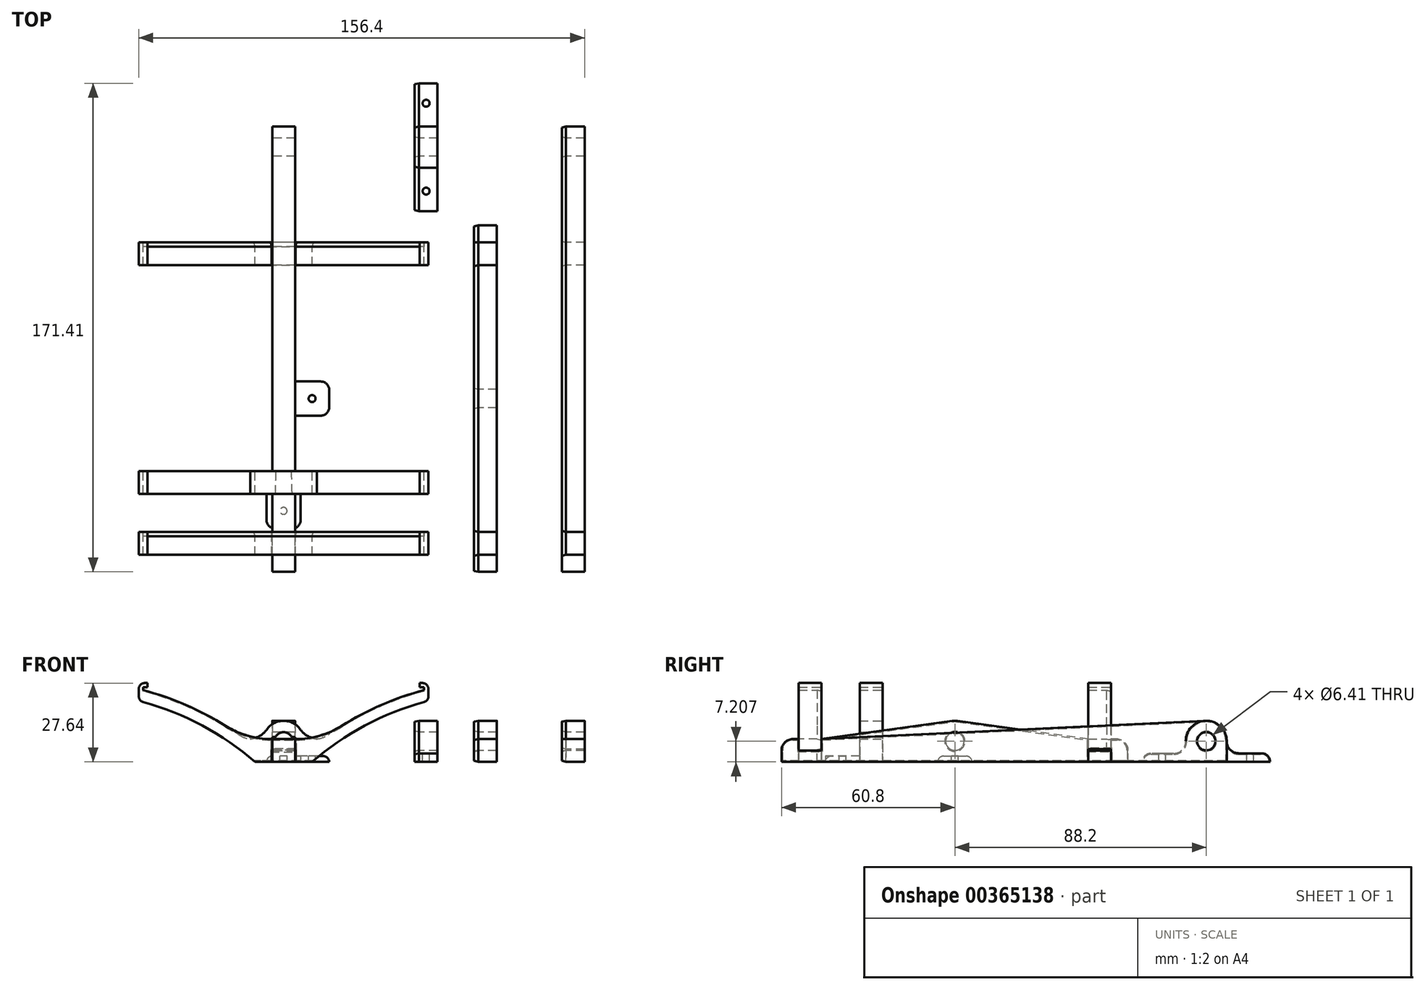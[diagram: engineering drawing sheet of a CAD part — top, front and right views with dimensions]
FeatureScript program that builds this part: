
annotation { "Feature Type Name" : "Feature", "Feature Type Description" : "" }
export const myFeature = defineFeature(function(context is Context, id is Id, definition is map)
    precondition{}
    {
        {
            assignVariable(context, id + "F0", {"name" : "frameWidth", "anyValue" : 101.6 * mm});
        }
        {
            assignVariable(context, id + "F1", {"name" : "picWidth", "anyValue" : 152.4 * mm});
        }
        {
            var Q0;
            Q0=qCreatedBy(makeId("Front.planeOp"),FACE);
            cPlane(context, id + "F2", {"entities" : qUnion([Q0]), "cplaneType" : CPlaneType.OFFSET, "offset" : getVariable(context, 'picWidth') / 6 * 5, "width" : 150 * mm, "height" : 150 * mm});
        }
        {
            var Q0;
            Q0=qCreatedBy(makeId("Front.planeOp"),FACE);
            cPlane(context, id + "F3", {"entities" : qUnion([Q0]), "cplaneType" : CPlaneType.OFFSET, "offset" : getVariable(context, 'picWidth') / 6, "width" : 150 * mm, "height" : 150 * mm});
        }
        {
            var Q0;
            Q0=qCreatedBy(makeId("Front.planeOp"),FACE);
            cPlane(context, id + "F4", {"entities" : qUnion([Q0]), "cplaneType" : CPlaneType.OFFSET, "offset" : getVariable(context, 'frameWidth'), "width" : 150 * mm, "height" : 150 * mm});
        }
        {
            var Q0;
            Q0=qCreatedBy(makeId("Right.planeOp"),FACE);
            cPlane(context, id + "F5", {"entities" : qUnion([Q0]), "cplaneType" : CPlaneType.OFFSET, "offset" : getVariable(context, 'frameWidth') / 2 + 20 * mm, "width" : 150 * mm, "height" : 150 * mm});
        }
        {
            var Q0;
            Q0=qCreatedBy(id+"F2.planeOp",FACE);
            var sketch = newSketch(context, id + "F6", { "sketchPlane" : qUnion([Q0])});
            skPoint(sketch, "E0", {"position": v(0, 0) * mm});
            skLineSegment(sketch, "E1", {"start": v(-49.3, 25.14) * mm, "end": v(-49.3, 26.14) * mm});
            skLineSegment(sketch, "E2", {"start": v(-49.3, 26.14) * mm, "end": v(-47.8, 26.14) * mm});
            skLineSegment(sketch, "E3", {"start": v(-47.8, 26.14) * mm, "end": v(-47.8, 27.64) * mm});
            skLineSegment(sketch, "E4", {"start": v(-47.8, 27.64) * mm, "end": v(-50.8, 27.64) * mm});
            skLineSegment(sketch, "E5", {"start": v(-50.8, 27.64) * mm, "end": v(-50.8, 21.4) * mm});
            skLineSegment(sketch, "E6", {"start": v(-13.57, 8) * mm, "end": v(0, 8) * mm});
            skLineSegment(sketch, "E7", {"start": v(-10, 0) * mm, "end": v(0, 0) * mm});
            skArc(sketch, "E8", {"start": v(-10, 0) * mm, "mid": v(-29.15, 13.08) * mm, "end": v(-50.8, 21.4) * mm});
            skArc(sketch, "E9.0", {"start": v(-13.57, 8) * mm, "mid": v(-30.61, 18.29) * mm, "end": v(-49.3, 25.14) * mm});
            skLineSegment(sketch, "E10.MirrorCS", {"start": v(49.3, 25.14) * mm, "end": v(49.3, 26.14) * mm});
            skLineSegment(sketch, "E11.MirrorCS", {"start": v(47.8, 26.14) * mm, "end": v(47.8, 27.64) * mm});
            skLineSegment(sketch, "E12.MirrorCS", {"start": v(49.3, 26.14) * mm, "end": v(47.8, 26.14) * mm});
            skLineSegment(sketch, "E13.MirrorCS", {"start": v(47.8, 27.64) * mm, "end": v(50.8, 27.64) * mm});
            skLineSegment(sketch, "E14.MirrorCS", {"start": v(10, 0) * mm, "end": v(0, 0) * mm});
            skLineSegment(sketch, "E15.MirrorCS", {"start": v(50.8, 27.64) * mm, "end": v(50.8, 21.4) * mm});
            skArc(sketch, "E16.MirrorCS", {"start": v(10, 0) * mm, "mid": v(29.15, 13.08) * mm, "end": v(50.8, 21.4) * mm});
            skArc(sketch, "E17.MirrorCS", {"start": v(13.57, 8) * mm, "mid": v(30.61, 18.29) * mm, "end": v(49.3, 25.14) * mm});
            skLineSegment(sketch, "E18.MirrorCS", {"start": v(13.57, 8) * mm, "end": v(0, 8) * mm});
            skLineSegment(sketch, "E19", {"start": v(-4.15, 0) * mm, "end": v(-4.15, 4.2) * mm});
            skLineSegment(sketch, "E20", {"start": v(-4.15, 4.2) * mm, "end": v(0, 4.2) * mm});
            skLineSegment(sketch, "E21.MirrorCS", {"start": v(4.15, 0) * mm, "end": v(4.15, 4.2) * mm});
            skLineSegment(sketch, "E22.MirrorCS", {"start": v(4.15, 4.2) * mm, "end": v(0, 4.2) * mm});
            skSolve(sketch);
        }
        {
            var Q0;
            Q0=qCreatedBy(id+"F3.planeOp",FACE);
            var sketch = newSketch(context, id + "F7", { "sketchPlane" : qUnion([Q0])});
            skLineSegment(sketch, "E23.0.0", {"start": v(4.15, 0) * mm, "end": v(10, 0) * mm});
            skArc(sketch, "E23.0.1", {"start": v(10, 0) * mm, "mid": v(29.15, 13.08) * mm, "end": v(50.8, 21.4) * mm});
            skLineSegment(sketch, "E23.0.2", {"start": v(50.8, 21.4) * mm, "end": v(50.8, 27.64) * mm});
            skLineSegment(sketch, "E23.0.3", {"start": v(50.8, 27.64) * mm, "end": v(47.8, 27.64) * mm});
            skLineSegment(sketch, "E23.0.4", {"start": v(47.8, 27.64) * mm, "end": v(47.8, 26.14) * mm});
            skLineSegment(sketch, "E23.0.5", {"start": v(47.8, 26.14) * mm, "end": v(49.3, 26.14) * mm});
            skLineSegment(sketch, "E23.0.6", {"start": v(49.3, 26.14) * mm, "end": v(49.3, 25.14) * mm});
            skArc(sketch, "E23.0.7", {"start": v(49.3, 25.14) * mm, "mid": v(30.61, 18.29) * mm, "end": v(13.57, 8) * mm});
            skLineSegment(sketch, "E23.0.8", {"start": v(13.57, 8) * mm, "end": v(0, 8) * mm});
            skLineSegment(sketch, "E23.0.9", {"start": v(0, 8) * mm, "end": v(-13.57, 8) * mm});
            skArc(sketch, "E23.0.10", {"start": v(-13.57, 8) * mm, "mid": v(-30.61, 18.29) * mm, "end": v(-49.3, 25.14) * mm});
            skLineSegment(sketch, "E23.0.11", {"start": v(-49.3, 25.14) * mm, "end": v(-49.3, 26.14) * mm});
            skLineSegment(sketch, "E23.0.12", {"start": v(-49.3, 26.14) * mm, "end": v(-47.8, 26.14) * mm});
            skLineSegment(sketch, "E23.0.13", {"start": v(-47.8, 26.14) * mm, "end": v(-47.8, 27.64) * mm});
            skLineSegment(sketch, "E23.0.14", {"start": v(-47.8, 27.64) * mm, "end": v(-50.8, 27.64) * mm});
            skLineSegment(sketch, "E23.0.15", {"start": v(-50.8, 27.64) * mm, "end": v(-50.8, 21.4) * mm});
            skArc(sketch, "E23.0.16", {"start": v(-50.8, 21.4) * mm, "mid": v(-29.15, 13.08) * mm, "end": v(-10, 0) * mm});
            skLineSegment(sketch, "E23.0.17", {"start": v(-10, 0) * mm, "end": v(-4.15, 0) * mm});
            skLineSegment(sketch, "E24", {"start": v(-4.15, 0) * mm, "end": v(4.15, 0) * mm});
            skLineSegment(sketch, "E25", {"start": v(-4.15, 8) * mm, "end": v(-4.15, 3.8) * mm});
            skLineSegment(sketch, "E26", {"start": v(-4.15, 3.8) * mm, "end": v(4.15, 3.8) * mm});
            skLineSegment(sketch, "E27", {"start": v(4.15, 3.8) * mm, "end": v(4.15, 8) * mm});
            skSolve(sketch);
        }
        {
            var Q0;
            Q0=makeQuery(id+"F6.imprint","IMPRINT",FACE,{"disambiguationData":[TD([[makeQuery(id+"F6.imprint","IMPRINT",EDGE,{"derivedFrom":sQuery(id+"F6.wireOp",EDGE,"E1")}),1.0]])]});
            extrude(context, id + "F8", {"entities" : qUnion([Q0]), "endBound" : BoundingType.SYMMETRIC, "depth" : 8 * mm});
        }
        {
            var Q0;
            Q0=makeQuery(id+"F7.imprint","IMPRINT",FACE,{"disambiguationData":[TD([[makeQuery(id+"F7.imprint","IMPRINT",EDGE,{"derivedFrom":sQuery(id+"F7.wireOp",EDGE,"E23.0.0")}),1.0]])]});
            extrude(context, id + "F9", {"entities" : qUnion([Q0]), "endBound" : BoundingType.SYMMETRIC, "depth" : 8 * mm});
        }
        {
            var Q0;
            Q0=makeQuery(id+"F8.opExtrude","SWEPT_EDGE",EDGE,{"disambiguationData":[OSD([sQuery(id+"F6.wireOp",EDGE,"0d4fdef2-052e-4615-a589-fe4d82cabcc1"),sQuery(id+"F6.wireOp",EDGE,"E5")])]});
            var Q1;
            Q1=makeQuery(id+"F8.opExtrude","SWEPT_EDGE",EDGE,{"disambiguationData":[OSD([sQuery(id+"F6.wireOp",EDGE,"9eb94c48-6d23-4655-9cba-3e0dd2628b4b0.MirrorCS"),sQuery(id+"F6.wireOp",EDGE,"d66b6ad6-a195-4717-835e-76c59413fe9c0.MirrorCS")])]});
            var Q2;
            Q2=makeQuery(id+"F8.opExtrude","SWEPT_EDGE",EDGE,{"disambiguationData":[OSD([sQuery(id+"F6.wireOp",EDGE,"E15.MirrorCS"),sQuery(id+"F6.wireOp",EDGE,"E16.MirrorCS")])]});
            var Q3;
            Q3=makeQuery(id+"F8.opExtrude","SWEPT_EDGE",EDGE,{"disambiguationData":[OSD([sQuery(id+"F6.wireOp",EDGE,"E13.MirrorCS"),sQuery(id+"F6.wireOp",EDGE,"E15.MirrorCS")])]});
            var Q4;
            Q4=makeQuery(id+"F9.opExtrude","SWEPT_EDGE",EDGE,{"disambiguationData":[OSD([sQuery(id+"F7.wireOp",EDGE,"E23.0.2"),sQuery(id+"F7.wireOp",EDGE,"E23.0.3")])]});
            var Q5;
            Q5=makeQuery(id+"F9.opExtrude","SWEPT_EDGE",EDGE,{"disambiguationData":[OSD([sQuery(id+"F7.wireOp",EDGE,"E23.0.1"),sQuery(id+"F7.wireOp",EDGE,"E23.0.2")])]});
            var Q6;
            Q6=makeQuery(id+"F9.opExtrude","SWEPT_EDGE",EDGE,{"disambiguationData":[OSD([sQuery(id+"F7.wireOp",EDGE,"E23.0.14"),sQuery(id+"F7.wireOp",EDGE,"E23.0.15")])]});
            var Q7;
            Q7=makeQuery(id+"F9.opExtrude","SWEPT_EDGE",EDGE,{"disambiguationData":[OSD([sQuery(id+"F7.wireOp",EDGE,"E23.0.15"),sQuery(id+"F7.wireOp",EDGE,"E23.0.16")])]});
            fillet(context, id + "F10", {"entities" : qUnion([Q0, Q1, Q2, Q3, Q4, Q5, Q6, Q7]), "radius" : 2 * mm, "tangentPropagation" : true, "allowEdgeOverflow" : false});
        }
        {
            var Q0;
            Q0=makeQuery(id+"F8.opExtrude","SWEPT_EDGE",EDGE,{"disambiguationData":[OSD([sQuery(id+"F6.wireOp",EDGE,"E17.MirrorCS"),sQuery(id+"F6.wireOp",EDGE,"E18.MirrorCS")])]});
            var Q1;
            Q1=makeQuery(id+"F8.opExtrude","SWEPT_EDGE",EDGE,{"disambiguationData":[OSD([sQuery(id+"F6.wireOp",EDGE,"E6"),sQuery(id+"F6.wireOp",EDGE,"E9.0")])]});
            var Q2;
            Q2=makeQuery(id+"F9.opExtrude","SWEPT_EDGE",EDGE,{"disambiguationData":[OSD([sQuery(id+"F7.wireOp",EDGE,"E23.0.7"),sQuery(id+"F7.wireOp",EDGE,"E23.0.8")])]});
            var Q3;
            Q3=makeQuery(id+"F9.opExtrude","SWEPT_EDGE",EDGE,{"disambiguationData":[OSD([sQuery(id+"F7.wireOp",EDGE,"E23.0.9"),sQuery(id+"F7.wireOp",EDGE,"E23.0.10")])]});
            fillet(context, id + "F11", {"entities" : qUnion([Q0, Q1, Q2, Q3]), "radius" : 30 * mm, "tangentPropagation" : true, "allowEdgeOverflow" : false});
        }
        {
            var Q0;
            Q0=qCreatedBy(makeId("Top.planeOp"),FACE);
            var sketch = newSketch(context, id + "F12", { "sketchPlane" : qUnion([Q0])});
            skLineSegment(sketch, "E28", {"start": v(-144.53, 0) * mm, "end": v(164.72, 0) * mm, "construction": true});
            skSolve(sketch);
        }
        {
            var Q0;
            Q0=qCreatedBy(makeId("Right.planeOp"),FACE);
            var sketch = newSketch(context, id + "F13", { "sketchPlane" : qUnion([Q0])});
            skPoint(sketch, "E29.0", {"position": v(0, 0) * mm});
            skLineSegment(sketch, "E30.0", {"start": v(-131, 3.9) * mm, "end": v(-131, 21.01) * mm});
            skLineSegment(sketch, "E31.0", {"start": v(-123, 3.9) * mm, "end": v(-123, 21.01) * mm});
            skLineSegment(sketch, "E32.bottom", {"start": v(-137, 0) * mm, "end": v(0, 0) * mm});
            skCircle(sketch, "E33", {"center": v(12, 7.2) * mm, "radius": 3.2 * mm});
            skLineSegment(sketch, "E34", {"start": v(-131, 3.9) * mm, "end": v(-123, 3.9) * mm});
            skPoint(sketch, "E35.orphan", {"position": v(-131, 0) * mm});
            skPoint(sketch, "E36.orphan", {"position": v(-123, 0) * mm});
            skLineSegment(sketch, "E37", {"start": v(-137, 8) * mm, "end": v(-137, 0) * mm});
            skPoint(sketch, "E38.0", {"position": v(-123, 8) * mm});
            skArc(sketch, "E39", {"start": v(19.2, 7.2) * mm, "mid": v(16.97, 12.42) * mm, "end": v(11.66, 14.4) * mm});
            skLineSegment(sketch, "E40", {"start": v(19.2, 7.2) * mm, "end": v(19.2, 0) * mm});
            skLineSegment(sketch, "E41", {"start": v(19.2, 0) * mm, "end": v(0, 0) * mm});
            skLineSegment(sketch, "E42", {"start": v(11.66, 14.4) * mm, "end": v(-123, 8) * mm});
            skPoint(sketch, "E43", {"position": v(-131, 8) * mm});
            skLineSegment(sketch, "E44", {"start": v(-131, 8) * mm, "end": v(-137, 8) * mm});
            skPoint(sketch, "E45.0", {"position": v(-25.4, 0) * mm});
            skLineSegment(sketch, "E46", {"start": v(-29.4, 4.5) * mm, "end": v(-21.4, 4.5) * mm});
            skPoint(sketch, "E47", {"position": v(-25.4, 4.5) * mm});
            skLineSegment(sketch, "E48", {"start": v(-29.4, 4.5) * mm, "end": v(-29.4, 0) * mm});
            skLineSegment(sketch, "E49", {"start": v(-21.4, 4.5) * mm, "end": v(-21.4, 0) * mm});
            skSolve(sketch);
        }
        {
            var Q0;
            Q0=qCreatedBy(id+"F4.planeOp",FACE);
            var sketch = newSketch(context, id + "F14", { "sketchPlane" : qUnion([Q0])});
            skLineSegment(sketch, "E50.0.0", {"start": v(4.15, 0) * mm, "end": v(10, 0) * mm});
            skArc(sketch, "E50.0.1", {"start": v(10, 0) * mm, "mid": v(29.15, 13.08) * mm, "end": v(50.8, 21.4) * mm});
            skLineSegment(sketch, "E50.0.2", {"start": v(50.8, 21.4) * mm, "end": v(50.8, 27.64) * mm});
            skLineSegment(sketch, "E50.0.3", {"start": v(50.8, 27.64) * mm, "end": v(47.8, 27.64) * mm});
            skLineSegment(sketch, "E50.0.4", {"start": v(47.8, 27.64) * mm, "end": v(47.8, 26.14) * mm});
            skLineSegment(sketch, "E50.0.5", {"start": v(47.8, 26.14) * mm, "end": v(49.3, 26.14) * mm});
            skLineSegment(sketch, "E50.0.6", {"start": v(49.3, 26.14) * mm, "end": v(49.3, 25.14) * mm});
            skArc(sketch, "E50.0.7", {"start": v(49.3, 25.14) * mm, "mid": v(30.61, 18.29) * mm, "end": v(13.57, 8) * mm});
            skLineSegment(sketch, "E50.0.8", {"start": v(13.57, 8) * mm, "end": v(7.16, 8) * mm});
            skLineSegment(sketch, "E50.0.9", {"start": v(-7.16, 8) * mm, "end": v(-13.57, 8) * mm});
            skArc(sketch, "E50.0.10", {"start": v(-13.57, 8) * mm, "mid": v(-30.61, 18.29) * mm, "end": v(-49.3, 25.14) * mm});
            skLineSegment(sketch, "E50.0.11", {"start": v(-49.3, 25.14) * mm, "end": v(-49.3, 26.14) * mm});
            skLineSegment(sketch, "E50.0.12", {"start": v(-49.3, 26.14) * mm, "end": v(-47.8, 26.14) * mm});
            skLineSegment(sketch, "E50.0.13", {"start": v(-47.8, 26.14) * mm, "end": v(-47.8, 27.64) * mm});
            skLineSegment(sketch, "E50.0.14", {"start": v(-47.8, 27.64) * mm, "end": v(-50.8, 27.64) * mm});
            skLineSegment(sketch, "E50.0.15", {"start": v(-50.8, 27.64) * mm, "end": v(-50.8, 21.4) * mm});
            skArc(sketch, "E50.0.16", {"start": v(-50.8, 21.4) * mm, "mid": v(-29.15, 13.08) * mm, "end": v(-10, 0) * mm});
            skLineSegment(sketch, "E50.0.17", {"start": v(-10, 0) * mm, "end": v(-4.15, 0) * mm});
            skLineSegment(sketch, "E51.0.1", {"start": v(-4.15, 0) * mm, "end": v(0, 0) * mm});
            skLineSegment(sketch, "E51.0.2", {"start": v(0, 0) * mm, "end": v(4.15, 0) * mm});
            skPoint(sketch, "E52.0", {"position": v(0, 7.2) * mm});
            skLineSegment(sketch, "E53.0", {"start": v(0, 10.41) * mm, "end": v(0, 4) * mm, "construction": true});
            skCircle(sketch, "E54", {"center": v(0, 7.2) * mm, "radius": 3.2 * mm});
            skArc(sketch, "E55", {"start": v(7.16, 8) * mm, "mid": v(0, 14.41) * mm, "end": v(-7.16, 8) * mm});
            skPoint(sketch, "E56.orphan", {"position": v(0, 8) * mm});
            skSolve(sketch);
        }
        {
            var Q0;
            Q0=makeQuery(id+"F14.imprint","IMPRINT",FACE,{"disambiguationData":[TD([[makeQuery(id+"F14.imprint","IMPRINT",EDGE,{"derivedFrom":sQuery(id+"F14.wireOp",EDGE,"E50.0.0")}),1.0]])]});
            extrude(context, id + "F15", {"entities" : qUnion([Q0]), "depth" : 8 * mm});
        }
        {
            var Q0;
            Q0=makeQuery(id+"F15.opExtrude","SWEPT_EDGE",EDGE,{"disambiguationData":[OSD([sQuery(id+"F14.wireOp",EDGE,"E50.0.15"),sQuery(id+"F14.wireOp",EDGE,"E50.0.16")])]});
            var Q1;
            Q1=makeQuery(id+"F15.opExtrude","SWEPT_EDGE",EDGE,{"disambiguationData":[OSD([sQuery(id+"F14.wireOp",EDGE,"E50.0.14"),sQuery(id+"F14.wireOp",EDGE,"E50.0.15")])]});
            var Q2;
            Q2=makeQuery(id+"F15.opExtrude","SWEPT_EDGE",EDGE,{"disambiguationData":[OSD([sQuery(id+"F14.wireOp",EDGE,"E50.0.1"),sQuery(id+"F14.wireOp",EDGE,"E50.0.2")])]});
            var Q3;
            Q3=makeQuery(id+"F15.opExtrude","SWEPT_EDGE",EDGE,{"disambiguationData":[OSD([sQuery(id+"F14.wireOp",EDGE,"E50.0.2"),sQuery(id+"F14.wireOp",EDGE,"E50.0.3")])]});
            fillet(context, id + "F16", {"entities" : qUnion([Q0, Q1, Q2, Q3]), "radius" : 2 * mm, "tangentPropagation" : true, "allowEdgeOverflow" : false});
        }
        {
            var Q0;
            Q0=makeQuery(id+"F15.opExtrude","SWEPT_EDGE",EDGE,{"disambiguationData":[OSD([sQuery(id+"F14.wireOp",EDGE,"E50.0.9"),sQuery(id+"F14.wireOp",EDGE,"E55")])]});
            var Q1;
            Q1=makeQuery(id+"F15.opExtrude","SWEPT_EDGE",EDGE,{"disambiguationData":[OSD([sQuery(id+"F14.wireOp",EDGE,"E50.0.8"),sQuery(id+"F14.wireOp",EDGE,"E55")])]});
            var Q2;
            Q2=makeQuery(id+"F15.opExtrude","SWEPT_EDGE",EDGE,{"disambiguationData":[OSD([sQuery(id+"F14.wireOp",EDGE,"E50.0.7"),sQuery(id+"F14.wireOp",EDGE,"E50.0.8")])]});
            var Q3;
            Q3=makeQuery(id+"F15.opExtrude","SWEPT_EDGE",EDGE,{"disambiguationData":[OSD([sQuery(id+"F14.wireOp",EDGE,"E50.0.9"),sQuery(id+"F14.wireOp",EDGE,"E50.0.10")])]});
            fillet(context, id + "F17", {"entities" : qUnion([Q0, Q1, Q2, Q3]), "radius" : 8 * mm, "tangentPropagation" : true, "allowEdgeOverflow" : false});
        }
        {
            var Q0;
            Q0=makeQuery(id+"F13.imprint","IMPRINT",FACE,{"disambiguationData":[TD([[makeQuery(id+"F13.imprint","IMPRINT",EDGE,{"derivedFrom":sQuery(id+"F13.wireOp",EDGE,"E33")}),-1.0]])]});
            var Q1;
            {var subQ0=sQuery(id+"F13.wireOp",EDGE,"WvEQeHSi-91Ns-riZe-GzQt-8XYZ8DeBNsEi");Q1=makeQuery(id+"F13.imprint","IMPRINT",FACE,{"disambiguationData":[TD([[makeQuery(id+"F13.imprint","IMPRINT",EDGE,{"derivedFrom":subQ0}),-1.0]])]});}
            extrude(context, id + "F18", {"entities" : qUnion([Q0, Q1]), "endBound" : BoundingType.SYMMETRIC, "depth" : 8 * mm});
        }
        {
            var Q0;
            Q0=makeQuery(id+"F18.opExtrude","SWEPT_EDGE",EDGE,{"disambiguationData":[OSD([sQuery(id+"F13.wireOp",EDGE,"E37"),sQuery(id+"F13.wireOp",EDGE,"E44")])]});
            fillet(context, id + "F19", {"entities" : qUnion([Q0]), "radius" : 4 * mm, "tangentPropagation" : true, "allowEdgeOverflow" : false});
        }
        {
            var Q0;
            Q0=qCreatedBy(id+"F5.planeOp",FACE);
            var sketch = newSketch(context, id + "F20", { "sketchPlane" : qUnion([Q0])});
            skLineSegment(sketch, "E57.0.7", {"start": v(-123, 8) * mm, "end": v(-123, 3.9) * mm});
            skLineSegment(sketch, "E57.0.8", {"start": v(-123, 3.9) * mm, "end": v(-131, 3.9) * mm});
            skLineSegment(sketch, "E57.0.9", {"start": v(-131, 3.9) * mm, "end": v(-131, 8) * mm});
            skLineSegment(sketch, "E57.0.10", {"start": v(-131, 8) * mm, "end": v(-137, 8) * mm});
            skLineSegment(sketch, "E57.0.11", {"start": v(-137, 8) * mm, "end": v(-137, 0) * mm});
            skCircle(sketch, "E58.0", {"center": v(12, 7.2) * mm, "radius": 3.2 * mm, "construction": true});
            skCircle(sketch, "E59", {"center": v(-76.2, 7.2) * mm, "radius": 3.2 * mm});
            skLineSegment(sketch, "E60", {"start": v(-76.2, 7.2) * mm, "end": v(-76.2, 42.57) * mm, "construction": true});
            skLineSegment(sketch, "E61.MirrorCS", {"start": v(-15.4, 8) * mm, "end": v(-15.4, 0) * mm});
            skLineSegment(sketch, "E62.MirrorCS", {"start": v(-21.4, 8) * mm, "end": v(-15.4, 8) * mm});
            skLineSegment(sketch, "E63.MirrorCS", {"start": v(-29.4, 3.9) * mm, "end": v(-21.4, 3.9) * mm});
            skLineSegment(sketch, "E64.MirrorCS", {"start": v(-29.4, 8) * mm, "end": v(-29.4, 3.9) * mm});
            skLineSegment(sketch, "E65.MirrorCS", {"start": v(-21.4, 3.9) * mm, "end": v(-21.4, 8) * mm});
            skLineSegment(sketch, "E66", {"start": v(-137, 0) * mm, "end": v(-15.4, 0) * mm});
            skArc(sketch, "E67", {"start": v(-75.21, 14.35) * mm, "mid": v(-76.2, 14.41) * mm, "end": v(-77.19, 14.35) * mm});
            skLineSegment(sketch, "E68", {"start": v(-123, 8) * mm, "end": v(-77.19, 14.35) * mm});
            skLineSegment(sketch, "E69", {"start": v(-29.4, 8) * mm, "end": v(-75.21, 14.35) * mm});
            skSolve(sketch);
        }
        {
            var Q0;
            Q0=makeQuery(id+"F20.imprint","IMPRINT",FACE,{"disambiguationData":[TD([[makeQuery(id+"F20.imprint","IMPRINT",EDGE,{"derivedFrom":sQuery(id+"F20.wireOp",EDGE,"E57.0.7")}),1.0]])]});
            extrude(context, id + "F21", {"entities" : qUnion([Q0]), "endBound" : BoundingType.SYMMETRIC, "depth" : 8 * mm});
        }
        {
            var Q0;
            Q0=makeQuery(id+"F21.opExtrude","SWEPT_EDGE",EDGE,{"disambiguationData":[OSD([sQuery(id+"F20.wireOp",EDGE,"E61.MirrorCS"),sQuery(id+"F20.wireOp",EDGE,"E62.MirrorCS")])]});
            var Q1;
            Q1=makeQuery(id+"F21.opExtrude","SWEPT_EDGE",EDGE,{"disambiguationData":[OSD([sQuery(id+"F20.wireOp",EDGE,"E57.0.10"),sQuery(id+"F20.wireOp",EDGE,"E57.0.11")])]});
            fillet(context, id + "F22", {"entities" : qUnion([Q0, Q1]), "radius" : 4 * mm, "tangentPropagation" : true, "allowEdgeOverflow" : false});
        }
        {
            var Q0;
            Q0=makeQuery(id+"F18.opExtrude","SWEPT_BODY",BODY,{"disambiguationData":[OSD([sQuery(id+"F13.wireOp",EDGE,"E30.0"),sQuery(id+"F13.wireOp",EDGE,"E31.0"),sQuery(id+"F13.wireOp",EDGE,"E32.bottom"),sQuery(id+"F13.wireOp",EDGE,"E33"),sQuery(id+"F13.wireOp",EDGE,"E34"),sQuery(id+"F13.wireOp",EDGE,"E37"),sQuery(id+"F13.wireOp",EDGE,"E39"),sQuery(id+"F13.wireOp",EDGE,"E40"),sQuery(id+"F13.wireOp",EDGE,"E41"),sQuery(id+"F13.wireOp",EDGE,"E42"),sQuery(id+"F13.wireOp",EDGE,"E44"),sQuery(id+"F13.wireOp",EDGE,"E46"),sQuery(id+"F13.wireOp",EDGE,"E48"),sQuery(id+"F13.wireOp",EDGE,"E49")])]});
            transform(context, id + "F23", {"entities" : qUnion([Q0]), "transformType" : TransformType.TRANSLATION_3D, "dx" : getVariable(context, 'frameWidth'), "dy" : 0 * mm, "dz" : 0 * mm, "makeCopy" : true});
        }
        {
            var Q0;
            Q0=makeQuery(id+"F18.opExtrude","CAP_FACE",FACE,{"disambiguationData":[OSD([sQuery(id+"F13.wireOp",EDGE,"E30.0"),sQuery(id+"F13.wireOp",EDGE,"E31.0"),sQuery(id+"F13.wireOp",EDGE,"E32.bottom"),sQuery(id+"F13.wireOp",EDGE,"E33"),sQuery(id+"F13.wireOp",EDGE,"E34"),sQuery(id+"F13.wireOp",EDGE,"E37"),sQuery(id+"F13.wireOp",EDGE,"E39"),sQuery(id+"F13.wireOp",EDGE,"E40"),sQuery(id+"F13.wireOp",EDGE,"E41"),sQuery(id+"F13.wireOp",EDGE,"E42"),sQuery(id+"F13.wireOp",EDGE,"E44"),sQuery(id+"F13.wireOp",EDGE,"E46"),sQuery(id+"F13.wireOp",EDGE,"E48"),sQuery(id+"F13.wireOp",EDGE,"E49")])],"isStart":false});
            var sketch = newSketch(context, id + "F24", { "sketchPlane" : qUnion([Q0])});
            skLineSegment(sketch, "E70.0.0", {"start": v(-21.4, 0) * mm, "end": v(3.18, 0) * mm});
            skLineSegment(sketch, "E70.0.4", {"start": v(-123, 3.99) * mm, "end": v(-123, 3.9) * mm});
            skLineSegment(sketch, "E70.0.6", {"start": v(-131, 3.9) * mm, "end": v(-131, 4) * mm});
            skLineSegment(sketch, "E70.0.9", {"start": v(-90.67, 0) * mm, "end": v(-29.4, 0) * mm});
            skLineSegment(sketch, "E70.0.10", {"start": v(-29.4, 0) * mm, "end": v(-29.4, 4.5) * mm});
            skLineSegment(sketch, "E70.0.11", {"start": v(-29.4, 4.5) * mm, "end": v(-21.4, 4.5) * mm});
            skLineSegment(sketch, "E70.0.12", {"start": v(-21.4, 4.5) * mm, "end": v(-21.4, 0) * mm});
            skPoint(sketch, "E71", {"position": v(-76.2, 0) * mm});
            skLineSegment(sketch, "E72", {"start": v(-82.2, 2) * mm, "end": v(-70.2, 2) * mm});
            skPoint(sketch, "E73", {"position": v(-76.2, 2) * mm});
            skLineSegment(sketch, "E74", {"start": v(-82.2, 2) * mm, "end": v(-82.2, 0) * mm});
            skLineSegment(sketch, "E75", {"start": v(-70.2, 2) * mm, "end": v(-70.2, 0) * mm});
            skSolve(sketch);
        }
        {
            var Q0;
            Q0=makeQuery(id+"F24.imprint","IMPRINT",FACE,{"disambiguationData":[TD([[makeQuery(id+"F24.imprint","IMPRINT",EDGE,{"derivedFrom":sQuery(id+"F24.wireOp",EDGE,"E72")}),-1.0]])]});
            extrude(context, id + "F25", {"entities" : qUnion([Q0]), "operationType" : NewBodyOperationType.ADD, "depth" : 12 * mm});
        }
        {
            var Q0;
            Q0=makeQuery(id+"F25.opExtrude","CAP_EDGE",EDGE,{"disambiguationData":[OSD([sQuery(id+"F24.wireOp",EDGE,"E74")])],"isStart":true});
            var Q1;
            Q1=makeQuery(id+"F25.opExtrude","CAP_EDGE",EDGE,{"disambiguationData":[OSD([sQuery(id+"F24.wireOp",EDGE,"E75")])],"isStart":true});
            var Q2;
            Q2=makeQuery(id+"F25.opExtrude","CAP_EDGE",EDGE,{"disambiguationData":[OSD([sQuery(id+"F24.wireOp",EDGE,"E72")])],"isStart":true});
            var Q3;
            Q3=makeQuery(id+"F25.opExtrude","CAP_EDGE",EDGE,{"disambiguationData":[OSD([sQuery(id+"F24.wireOp",EDGE,"E74")])],"isStart":false});
            var Q4;
            Q4=makeQuery(id+"F25.opExtrude","CAP_EDGE",EDGE,{"disambiguationData":[OSD([sQuery(id+"F24.wireOp",EDGE,"E75")])],"isStart":false});
            fillet(context, id + "F26", {"entities" : qUnion([Q0, Q1, Q2, Q3, Q4]), "radius" : 3 * mm, "tangentPropagation" : true, "allowEdgeOverflow" : false});
        }
        {
            var Q0;
            Q0=makeQuery(id+"F25.opExtrude","SWEPT_EDGE",EDGE,{"disambiguationData":[OSD([sQuery(id+"F24.wireOp",EDGE,"E72"),sQuery(id+"F24.wireOp",EDGE,"E74")])]});
            fillet(context, id + "F27", {"entities" : qUnion([Q0]), "radius" : 2 * mm, "tangentPropagation" : true, "allowEdgeOverflow" : false});
        }
        {
            var Q0;
            Q0=makeQuery(id+"F25.opExtrude","SWEPT_FACE",FACE,{"disambiguationData":[OSD([sQuery(id+"F24.wireOp",EDGE,"E72")])]});
            var sketch = newSketch(context, id + "F28", { "sketchPlane" : qUnion([Q0])});
            skPoint(sketch, "E76", {"position": v(10, -76.2) * mm});
            skPoint(sketch, "E76.positionSnap0", {"position": v(7, -76.2) * mm});
            skPoint(sketch, "E76.positionSnap1", {"position": v(10, -80.2) * mm});
            skSolve(sketch);
        }
        {
            var Q0;
            Q0=qCreatedBy(makeId("Right.planeOp"),FACE);
            var sketch = newSketch(context, id + "F29", { "sketchPlane" : qUnion([Q0])});
            skCircle(sketch, "E77.0", {"center": v(12, 7.2) * mm, "radius": 3.2 * mm});
            skPoint(sketch, "E78", {"position": v(0, 0) * mm});
            skLineSegment(sketch, "E79", {"start": v(4.8, 7.2) * mm, "end": v(26, 7.2) * mm, "construction": true});
            skLineSegment(sketch, "E80", {"start": v(-10.41, 0) * mm, "end": v(12, 0) * mm});
            skPoint(sketch, "E81", {"position": v(12, 0) * mm});
            skLineSegment(sketch, "E82", {"start": v(-7.41, 3) * mm, "end": v(0.59, 3) * mm});
            skArc(sketch, "E83", {"start": v(0.59, 3) * mm, "mid": v(3.56, 4.23) * mm, "end": v(4.8, 7.2) * mm});
            skArc(sketch, "E84", {"start": v(-7.41, 3) * mm, "mid": v(-9.53, 2.12) * mm, "end": v(-10.41, 0) * mm});
            skLineSegment(sketch, "E85", {"start": v(12, 7.2) * mm, "end": v(12, 17.28) * mm, "construction": true});
            skArc(sketch, "E86.MirrorCS", {"start": v(23.41, 3) * mm, "mid": v(20.44, 4.23) * mm, "end": v(19.2, 7.2) * mm});
            skLineSegment(sketch, "E87.MirrorCS", {"start": v(31.41, 3) * mm, "end": v(23.41, 3) * mm});
            skArc(sketch, "E88.MirrorCS", {"start": v(31.41, 3) * mm, "mid": v(33.53, 2.12) * mm, "end": v(34.41, 0) * mm});
            skLineSegment(sketch, "E89.MirrorCS", {"start": v(34.41, 0) * mm, "end": v(12, 0) * mm});
            skArc(sketch, "E90", {"start": v(19.2, 7.2) * mm, "mid": v(12, 14.41) * mm, "end": v(4.8, 7.2) * mm});
            skSolve(sketch);
        }
        {
            var Q0;
            Q0=makeQuery(id+"F29.imprint","IMPRINT",FACE,{"disambiguationData":[TD([[makeQuery(id+"F29.imprint","IMPRINT",EDGE,{"derivedFrom":sQuery(id+"F29.wireOp",EDGE,"E77.0")}),-1.0]])]});
            extrude(context, id + "F30", {"entities" : qUnion([Q0]), "endBound" : BoundingType.SYMMETRIC, "depth" : 8 * mm});
        }
        {
            var Q0;
            Q0=makeQuery(id+"F30.opExtrude","SWEPT_BODY",BODY,{"disambiguationData":[OSD([sQuery(id+"F29.wireOp",EDGE,"E77.0"),sQuery(id+"F29.wireOp",EDGE,"672XMrIM-QfOK-u1MF-bKZu-H5Uik9iDEu2a"),sQuery(id+"F29.wireOp",EDGE,"on8Fqwfm-eHCa-UyCz-5yqo-W9CwT8bCkcOa"),sQuery(id+"F29.wireOp",EDGE,"zkd6ojhd-7DSJ-bBkh-u00N-I2pNIaye94sp"),sQuery(id+"F29.wireOp",EDGE,"1G0Aqs78-1kBY-28fw-sgL4-J5HLA91RHUUv"),sQuery(id+"F29.wireOp",EDGE,"kuRzcjOL-MatJ-vrTS-F3nu-ejoqISNA8lAi"),sQuery(id+"F29.wireOp",EDGE,"wWwTX445-3m2U-kflx-acxV-hRjx5SrFnte5"),sQuery(id+"F29.wireOp",EDGE,"087uxOaK-4sUk-eTGQ-OWXO-epjOHxzNvmRQ"),sQuery(id+"F29.wireOp",EDGE,"359a3ba5-355d-4b47-a863-6aaa0f1753870.MirrorCS"),sQuery(id+"F29.wireOp",EDGE,"f92cff40-58ed-4135-8013-71d5b81e02400.MirrorCS"),sQuery(id+"F29.wireOp",EDGE,"8e19f2e5-6a1e-400b-807b-bf6e4084e40a.trimOffspring")])]});
            transform(context, id + "F31", {"entities" : qUnion([Q0]), "transformType" : TransformType.TRANSLATION_3D, "dx" : 50 * mm, "dy" : 0 * mm, "dz" : 0 * mm, "makeCopy" : false});
        }
        {
            var Q0;
            Q0=makeQuery(id+"F30.opExtrude","SWEPT_FACE",FACE,{"disambiguationData":[OSD([sQuery(id+"F29.wireOp",EDGE,"E87.MirrorCS")])]});
            var sketch = newSketch(context, id + "F32", { "sketchPlane" : qUnion([Q0])});
            skLineSegment(sketch, "E91.0.0", {"start": v(46, 0.59) * mm, "end": v(46, -7.41) * mm, "construction": true});
            skLineSegment(sketch, "E91.0.1", {"start": v(46, -7.41) * mm, "end": v(54, -7.41) * mm, "construction": true});
            skLineSegment(sketch, "E91.0.2", {"start": v(54, -7.41) * mm, "end": v(54, 0.59) * mm, "construction": true});
            skLineSegment(sketch, "E91.0.3", {"start": v(54, 0.59) * mm, "end": v(46, 0.59) * mm, "construction": true});
            skLineSegment(sketch, "E92.0.0", {"start": v(46, 31.41) * mm, "end": v(46, 23.41) * mm, "construction": true});
            skLineSegment(sketch, "E92.0.1", {"start": v(46, 23.41) * mm, "end": v(54, 23.41) * mm, "construction": true});
            skLineSegment(sketch, "E92.0.2", {"start": v(54, 23.41) * mm, "end": v(54, 31.41) * mm, "construction": true});
            skLineSegment(sketch, "E92.0.3", {"start": v(54, 31.41) * mm, "end": v(46, 31.41) * mm, "construction": true});
            skPoint(sketch, "E93", {"position": v(50, -3.41) * mm});
            skPoint(sketch, "E93.positionSnap0", {"position": v(50, 0.59) * mm});
            skPoint(sketch, "E93.positionSnap1", {"position": v(46, -3.41) * mm});
            skPoint(sketch, "E94", {"position": v(50, 27.41) * mm});
            skPoint(sketch, "E94.positionSnap0", {"position": v(46, 27.41) * mm});
            skSolve(sketch);
        }
        {
            var Q0;
            Q0=makeQuery(id+"F15.opExtrude","CAP_FACE",FACE,{"disambiguationData":[OSD([sQuery(id+"F14.wireOp",EDGE,"E50.0.0"),sQuery(id+"F14.wireOp",EDGE,"E50.0.1"),sQuery(id+"F14.wireOp",EDGE,"E50.0.2"),sQuery(id+"F14.wireOp",EDGE,"E50.0.3"),sQuery(id+"F14.wireOp",EDGE,"E50.0.4"),sQuery(id+"F14.wireOp",EDGE,"E50.0.5"),sQuery(id+"F14.wireOp",EDGE,"E50.0.6"),sQuery(id+"F14.wireOp",EDGE,"E50.0.7"),sQuery(id+"F14.wireOp",EDGE,"E50.0.8"),sQuery(id+"F14.wireOp",EDGE,"E50.0.9"),sQuery(id+"F14.wireOp",EDGE,"E50.0.10"),sQuery(id+"F14.wireOp",EDGE,"E50.0.11"),sQuery(id+"F14.wireOp",EDGE,"E50.0.12"),sQuery(id+"F14.wireOp",EDGE,"E50.0.13"),sQuery(id+"F14.wireOp",EDGE,"E50.0.14"),sQuery(id+"F14.wireOp",EDGE,"E50.0.15"),sQuery(id+"F14.wireOp",EDGE,"E50.0.16"),sQuery(id+"F14.wireOp",EDGE,"E50.0.17"),sQuery(id+"F14.wireOp",EDGE,"E51.0.1"),sQuery(id+"F14.wireOp",EDGE,"E51.0.2"),sQuery(id+"F14.wireOp",EDGE,"E54"),sQuery(id+"F14.wireOp",EDGE,"E55")])],"isStart":false});
            var sketch = newSketch(context, id + "F33", { "sketchPlane" : qUnion([Q0])});
            skLineSegment(sketch, "E95", {"start": v(-6, 2) * mm, "end": v(6, 2) * mm});
            skPoint(sketch, "E96", {"position": v(0, 2) * mm});
            skLineSegment(sketch, "E97", {"start": v(-6, 2) * mm, "end": v(-6, 0) * mm});
            skLineSegment(sketch, "E98", {"start": v(6, 2) * mm, "end": v(6, 0) * mm});
            skSolve(sketch);
        }
        {
            var Q0;
            Q0=makeQuery(id+"F33.imprint","IMPRINT",FACE,{"disambiguationData":[TD([[makeQuery(id+"F33.imprint","IMPRINT",EDGE,{"derivedFrom":sQuery(id+"F33.wireOp",EDGE,"E95")}),-1.0]])]});
            extrude(context, id + "F34", {"entities" : qUnion([Q0]), "operationType" : NewBodyOperationType.ADD, "depth" : 12 * mm});
        }
        {
            var Q0;
            Q0=makeQuery(id+"F34.opExtrude","CAP_EDGE",EDGE,{"disambiguationData":[OSD([sQuery(id+"F33.wireOp",EDGE,"E97")])],"isStart":true});
            var Q1;
            Q1=makeQuery(id+"F34.opExtrude","CAP_EDGE",EDGE,{"disambiguationData":[OSD([sQuery(id+"F33.wireOp",EDGE,"E95")])],"isStart":true});
            var Q2;
            Q2=makeQuery(id+"F34.opExtrude","CAP_EDGE",EDGE,{"disambiguationData":[OSD([sQuery(id+"F33.wireOp",EDGE,"E98")])],"isStart":true});
            var Q3;
            Q3=makeQuery(id+"F34.opExtrude","CAP_EDGE",EDGE,{"disambiguationData":[OSD([sQuery(id+"F33.wireOp",EDGE,"E98")])],"isStart":false});
            var Q4;
            Q4=makeQuery(id+"F34.opExtrude","CAP_EDGE",EDGE,{"disambiguationData":[OSD([sQuery(id+"F33.wireOp",EDGE,"E97")])],"isStart":false});
            fillet(context, id + "F35", {"entities" : qUnion([Q0, Q1, Q2, Q3, Q4]), "radius" : 3 * mm, "tangentPropagation" : true, "allowEdgeOverflow" : false});
        }
        {
            var Q0;
            Q0=makeQuery(id+"F34.opExtrude","SWEPT_EDGE",EDGE,{"disambiguationData":[OSD([sQuery(id+"F33.wireOp",EDGE,"E95"),sQuery(id+"F33.wireOp",EDGE,"E97")])]});
            fillet(context, id + "F36", {"entities" : qUnion([Q0]), "radius" : 2 * mm, "tangentPropagation" : true, "allowEdgeOverflow" : false});
        }
        {
            var Q0;
            Q0=makeQuery(id+"F34.opExtrude","SWEPT_FACE",FACE,{"disambiguationData":[OSD([sQuery(id+"F33.wireOp",EDGE,"E95")])]});
            var sketch = newSketch(context, id + "F37", { "sketchPlane" : qUnion([Q0])});
            skPoint(sketch, "E99", {"position": v(0, -115.6) * mm});
            skPoint(sketch, "E99.positionSnap0", {"position": v(0, -119.6) * mm});
            skPoint(sketch, "E99.positionSnap1", {"position": v(-4, -115.6) * mm});
            skSolve(sketch);
        }
        {
            var Q0;
            Q0=sQuery(id+"F37.wireOp",VERTEX,"E99");
            var Q1;
            Q1=sQuery(id+"F32.wireOp",VERTEX,"E93");
            var Q2;
            Q2=sQuery(id+"F32.wireOp",VERTEX,"E94");
            var Q3;
            Q3=sQuery(id+"F28.wireOp",VERTEX,"E76");
            var Q4;
            Q4=makeQuery(id+"F30.opExtrude","SWEPT_BODY",BODY,{"disambiguationData":[OSD([sQuery(id+"F29.wireOp",EDGE,"E77.0"),sQuery(id+"F29.wireOp",EDGE,"672XMrIM-QfOK-u1MF-bKZu-H5Uik9iDEu2a"),sQuery(id+"F29.wireOp",EDGE,"on8Fqwfm-eHCa-UyCz-5yqo-W9CwT8bCkcOa"),sQuery(id+"F29.wireOp",EDGE,"zkd6ojhd-7DSJ-bBkh-u00N-I2pNIaye94sp"),sQuery(id+"F29.wireOp",EDGE,"1G0Aqs78-1kBY-28fw-sgL4-J5HLA91RHUUv"),sQuery(id+"F29.wireOp",EDGE,"kuRzcjOL-MatJ-vrTS-F3nu-ejoqISNA8lAi"),sQuery(id+"F29.wireOp",EDGE,"wWwTX445-3m2U-kflx-acxV-hRjx5SrFnte5"),sQuery(id+"F29.wireOp",EDGE,"087uxOaK-4sUk-eTGQ-OWXO-epjOHxzNvmRQ"),sQuery(id+"F29.wireOp",EDGE,"359a3ba5-355d-4b47-a863-6aaa0f1753870.MirrorCS"),sQuery(id+"F29.wireOp",EDGE,"f92cff40-58ed-4135-8013-71d5b81e02400.MirrorCS"),sQuery(id+"F29.wireOp",EDGE,"8e19f2e5-6a1e-400b-807b-bf6e4084e40a.trimOffspring")])]});
            var Q5;
            Q5=makeQuery(id+"F18.opExtrude","SWEPT_BODY",BODY,{"disambiguationData":[OSD([sQuery(id+"F13.wireOp",EDGE,"E30.0"),sQuery(id+"F13.wireOp",EDGE,"E31.0"),sQuery(id+"F13.wireOp",EDGE,"E32.bottom"),sQuery(id+"F13.wireOp",EDGE,"E33"),sQuery(id+"F13.wireOp",EDGE,"E34"),sQuery(id+"F13.wireOp",EDGE,"E37"),sQuery(id+"F13.wireOp",EDGE,"E39"),sQuery(id+"F13.wireOp",EDGE,"E40"),sQuery(id+"F13.wireOp",EDGE,"E41"),sQuery(id+"F13.wireOp",EDGE,"E42"),sQuery(id+"F13.wireOp",EDGE,"E44"),sQuery(id+"F13.wireOp",EDGE,"E46"),sQuery(id+"F13.wireOp",EDGE,"E48"),sQuery(id+"F13.wireOp",EDGE,"E49")])]});
            var Q6;
            Q6=makeQuery(id+"F15.opExtrude","SWEPT_BODY",BODY,{"disambiguationData":[OSD([sQuery(id+"F14.wireOp",EDGE,"E50.0.0"),sQuery(id+"F14.wireOp",EDGE,"E50.0.1"),sQuery(id+"F14.wireOp",EDGE,"E50.0.2"),sQuery(id+"F14.wireOp",EDGE,"E50.0.3"),sQuery(id+"F14.wireOp",EDGE,"E50.0.4"),sQuery(id+"F14.wireOp",EDGE,"E50.0.5"),sQuery(id+"F14.wireOp",EDGE,"E50.0.6"),sQuery(id+"F14.wireOp",EDGE,"E50.0.7"),sQuery(id+"F14.wireOp",EDGE,"E50.0.8"),sQuery(id+"F14.wireOp",EDGE,"E50.0.9"),sQuery(id+"F14.wireOp",EDGE,"E50.0.10"),sQuery(id+"F14.wireOp",EDGE,"E50.0.11"),sQuery(id+"F14.wireOp",EDGE,"E50.0.12"),sQuery(id+"F14.wireOp",EDGE,"E50.0.13"),sQuery(id+"F14.wireOp",EDGE,"E50.0.14"),sQuery(id+"F14.wireOp",EDGE,"E50.0.15"),sQuery(id+"F14.wireOp",EDGE,"E50.0.16"),sQuery(id+"F14.wireOp",EDGE,"E50.0.17"),sQuery(id+"F14.wireOp",EDGE,"E51.0.1"),sQuery(id+"F14.wireOp",EDGE,"E51.0.2"),sQuery(id+"F14.wireOp",EDGE,"E54"),sQuery(id+"F14.wireOp",EDGE,"E55")])]});
            hole(context, id + "F38", {"style" : HoleStyle.SIMPLE, "endStyle" : HoleEndStyle.THROUGH, "standardTappedOrClearance" : lookupTablePath({ "standard" : "ANSI", "fit" : "Normal (ASME)", "size" : "#2", "type" : "Clearance" }), "standardBlindInLast" : lookupTablePath({ "fit" : "Free", "standard" : "ANSI", "size" : "#2", "type" : "Clearance" }), "holeDiameter" : 2.44 * mm, "isTappedThrough" : true, "tappedDepth" : 12 * mm, "tapClearance" : 3, "locations" : qUnion([Q0, Q1, Q2, Q3]), "scope" : qUnion([Q4, Q5, Q6])});
        }
        {
            var Q0;
            Q0=makeQuery(id+"F8.opExtrude","CAP_EDGE",EDGE,{"disambiguationData":[OSD([sQuery(id+"F6.wireOp",EDGE,"E7")])],"isStart":true});
            var Q1;
            Q1=makeQuery(id+"F8.opExtrude","CAP_EDGE",EDGE,{"disambiguationData":[OSD([sQuery(id+"F6.wireOp",EDGE,"E14.MirrorCS")])],"isStart":true});
            var Q2;
            Q2=makeQuery(id+"F8.opExtrude","CAP_EDGE",EDGE,{"disambiguationData":[OSD([sQuery(id+"F6.wireOp",EDGE,"E21.MirrorCS")])],"isStart":true});
            var Q3;
            Q3=makeQuery(id+"F8.opExtrude","CAP_EDGE",EDGE,{"disambiguationData":[OSD([sQuery(id+"F6.wireOp",EDGE,"E20"),sQuery(id+"F6.wireOp",EDGE,"E22.MirrorCS")])],"isStart":true});
            var Q4;
            Q4=makeQuery(id+"F8.opExtrude","CAP_EDGE",EDGE,{"disambiguationData":[OSD([sQuery(id+"F6.wireOp",EDGE,"E19")])],"isStart":true});
            var Q5;
            Q5=makeQuery(id+"F9.opExtrude","CAP_EDGE",EDGE,{"disambiguationData":[OSD([sQuery(id+"F7.wireOp",EDGE,"E23.0.0"),sQuery(id+"F7.wireOp",EDGE,"E23.0.17"),sQuery(id+"F7.wireOp",EDGE,"E24")])],"isStart":true});
            var Q6;
            Q6=makeQuery(id+"F9.opExtrude","CAP_EDGE",EDGE,{"disambiguationData":[OSD([sQuery(id+"F7.wireOp",EDGE,"E23.0.10")])],"isStart":true});
            var Q7;
            {var subQ0=sQuery(id+"F7.wireOp",EDGE,"E23.0.8");var subQ1=sQuery(id+"F7.wireOp",EDGE,"E23.0.7");Q7=makeQuery(id+"F11.opFillet","BLEND_EDGE",EDGE,{"blendedFrom":[makeQuery(id+"F9.opExtrude","SWEPT_EDGE",EDGE,{"disambiguationData":[OSD([subQ1,subQ0])]}),makeQuery(id+"F9.opExtrude","CAP_FACE",FACE,{"disambiguationData":[OSD([sQuery(id+"F7.wireOp",EDGE,"E23.0.0"),sQuery(id+"F7.wireOp",EDGE,"E23.0.1"),sQuery(id+"F7.wireOp",EDGE,"E23.0.2"),sQuery(id+"F7.wireOp",EDGE,"E23.0.3"),sQuery(id+"F7.wireOp",EDGE,"E23.0.4"),sQuery(id+"F7.wireOp",EDGE,"E23.0.5"),sQuery(id+"F7.wireOp",EDGE,"E23.0.6"),subQ1,subQ0,sQuery(id+"F7.wireOp",EDGE,"E23.0.9"),sQuery(id+"F7.wireOp",EDGE,"E23.0.10"),sQuery(id+"F7.wireOp",EDGE,"E23.0.11"),sQuery(id+"F7.wireOp",EDGE,"E23.0.12"),sQuery(id+"F7.wireOp",EDGE,"E23.0.13"),sQuery(id+"F7.wireOp",EDGE,"E23.0.14"),sQuery(id+"F7.wireOp",EDGE,"E23.0.15"),sQuery(id+"F7.wireOp",EDGE,"E23.0.16"),sQuery(id+"F7.wireOp",EDGE,"E23.0.17"),sQuery(id+"F7.wireOp",EDGE,"E24"),sQuery(id+"F7.wireOp",EDGE,"E25"),sQuery(id+"F7.wireOp",EDGE,"E26"),sQuery(id+"F7.wireOp",EDGE,"E27")])],"isStart":true})],"blendedInto":[makeQuery(id+"F9.opExtrude","CAP_FACE",FACE,{"disambiguationData":[OSD([sQuery(id+"F7.wireOp",EDGE,"E23.0.0"),sQuery(id+"F7.wireOp",EDGE,"E23.0.1"),sQuery(id+"F7.wireOp",EDGE,"E23.0.2"),sQuery(id+"F7.wireOp",EDGE,"E23.0.3"),sQuery(id+"F7.wireOp",EDGE,"E23.0.4"),sQuery(id+"F7.wireOp",EDGE,"E23.0.5"),sQuery(id+"F7.wireOp",EDGE,"E23.0.6"),subQ1,subQ0,sQuery(id+"F7.wireOp",EDGE,"E23.0.9"),sQuery(id+"F7.wireOp",EDGE,"E23.0.10"),sQuery(id+"F7.wireOp",EDGE,"E23.0.11"),sQuery(id+"F7.wireOp",EDGE,"E23.0.12"),sQuery(id+"F7.wireOp",EDGE,"E23.0.13"),sQuery(id+"F7.wireOp",EDGE,"E23.0.14"),sQuery(id+"F7.wireOp",EDGE,"E23.0.15"),sQuery(id+"F7.wireOp",EDGE,"E23.0.16"),sQuery(id+"F7.wireOp",EDGE,"E23.0.17"),sQuery(id+"F7.wireOp",EDGE,"E24"),sQuery(id+"F7.wireOp",EDGE,"E25"),sQuery(id+"F7.wireOp",EDGE,"E26"),sQuery(id+"F7.wireOp",EDGE,"E27")])],"isStart":true})]});}
            var Q8;
            Q8=makeQuery(id+"F9.opExtrude","CAP_EDGE",EDGE,{"disambiguationData":[OSD([sQuery(id+"F7.wireOp",EDGE,"E27")])],"isStart":true});
            var Q9;
            Q9=makeQuery(id+"F9.opExtrude","CAP_EDGE",EDGE,{"disambiguationData":[OSD([sQuery(id+"F7.wireOp",EDGE,"E26")])],"isStart":true});
            var Q10;
            Q10=makeQuery(id+"F9.opExtrude","CAP_EDGE",EDGE,{"disambiguationData":[OSD([sQuery(id+"F7.wireOp",EDGE,"E25")])],"isStart":true});
            var Q11;
            Q11=makeQuery(id+"F8.opExtrude","CAP_EDGE",EDGE,{"disambiguationData":[OSD([sQuery(id+"F6.wireOp",EDGE,"E17.MirrorCS")])],"isStart":true});
            var Q12;
            Q12=makeQuery(id+"F15.opExtrude","CAP_EDGE",EDGE,{"disambiguationData":[OSD([sQuery(id+"F14.wireOp",EDGE,"E50.0.0"),sQuery(id+"F14.wireOp",EDGE,"E50.0.17"),sQuery(id+"F14.wireOp",EDGE,"E51.0.1"),sQuery(id+"F14.wireOp",EDGE,"E51.0.2")])],"isStart":true});
            var Q13;
            Q13=makeQuery(id+"F15.opExtrude","CAP_EDGE",EDGE,{"disambiguationData":[OSD([sQuery(id+"F14.wireOp",EDGE,"E54")])],"isStart":true});
            var Q14;
            Q14=makeQuery(id+"F18.opExtrude","CAP_EDGE",EDGE,{"disambiguationData":[OSD([sQuery(id+"F13.wireOp",EDGE,"E42")])],"isStart":true});
            var Q15;
            Q15=makeQuery(id+"F18.opExtrude","CAP_EDGE",EDGE,{"disambiguationData":[OSD([sQuery(id+"F13.wireOp",EDGE,"E31.0")])],"isStart":true});
            var Q16;
            Q16=makeQuery(id+"F18.opExtrude","CAP_EDGE",EDGE,{"disambiguationData":[OSD([sQuery(id+"F13.wireOp",EDGE,"E34")])],"isStart":true});
            var Q17;
            Q17=makeQuery(id+"F18.opExtrude","CAP_EDGE",EDGE,{"disambiguationData":[OSD([sQuery(id+"F13.wireOp",EDGE,"E30.0")])],"isStart":true});
            var Q18;
            Q18=makeQuery(id+"F18.opExtrude","CAP_EDGE",EDGE,{"disambiguationData":[OSD([sQuery(id+"F13.wireOp",EDGE,"E32.bottom")])],"isStart":true});
            var Q19;
            Q19=makeQuery(id+"F18.opExtrude","CAP_EDGE",EDGE,{"disambiguationData":[OSD([sQuery(id+"F13.wireOp",EDGE,"E48")])],"isStart":true});
            var Q20;
            Q20=makeQuery(id+"F18.opExtrude","CAP_EDGE",EDGE,{"disambiguationData":[OSD([sQuery(id+"F13.wireOp",EDGE,"E46")])],"isStart":true});
            var Q21;
            Q21=makeQuery(id+"F18.opExtrude","CAP_EDGE",EDGE,{"disambiguationData":[OSD([sQuery(id+"F13.wireOp",EDGE,"E49")])],"isStart":true});
            var Q22;
            Q22=makeQuery(id+"F18.opExtrude","CAP_EDGE",EDGE,{"disambiguationData":[OSD([sQuery(id+"F13.wireOp",EDGE,"E32.bottom"),sQuery(id+"F13.wireOp",EDGE,"E41")])],"isStart":true});
            var Q23;
            Q23=makeQuery(id+"F18.opExtrude","CAP_EDGE",EDGE,{"disambiguationData":[OSD([sQuery(id+"F13.wireOp",EDGE,"E33")])],"isStart":true});
            var Q24;
            Q24=makeQuery(id+"F21.opExtrude","CAP_EDGE",EDGE,{"disambiguationData":[OSD([sQuery(id+"F20.wireOp",EDGE,"E69")])],"isStart":true});
            var Q25;
            Q25=makeQuery(id+"F21.opExtrude","CAP_EDGE",EDGE,{"disambiguationData":[OSD([sQuery(id+"F20.wireOp",EDGE,"E64.MirrorCS")])],"isStart":true});
            var Q26;
            Q26=makeQuery(id+"F21.opExtrude","CAP_EDGE",EDGE,{"disambiguationData":[OSD([sQuery(id+"F20.wireOp",EDGE,"E63.MirrorCS")])],"isStart":true});
            var Q27;
            Q27=makeQuery(id+"F21.opExtrude","CAP_EDGE",EDGE,{"disambiguationData":[OSD([sQuery(id+"F20.wireOp",EDGE,"E62.MirrorCS")])],"isStart":true});
            var Q28;
            Q28=makeQuery(id+"F21.opExtrude","CAP_EDGE",EDGE,{"disambiguationData":[OSD([sQuery(id+"F20.wireOp",EDGE,"E57.0.7")])],"isStart":true});
            var Q29;
            Q29=makeQuery(id+"F21.opExtrude","CAP_EDGE",EDGE,{"disambiguationData":[OSD([sQuery(id+"F20.wireOp",EDGE,"E57.0.8")])],"isStart":true});
            var Q30;
            Q30=makeQuery(id+"F21.opExtrude","CAP_EDGE",EDGE,{"disambiguationData":[OSD([sQuery(id+"F20.wireOp",EDGE,"E57.0.9")])],"isStart":true});
            var Q31;
            Q31=makeQuery(id+"F21.opExtrude","CAP_EDGE",EDGE,{"disambiguationData":[OSD([sQuery(id+"F20.wireOp",EDGE,"E57.0.10")])],"isStart":true});
            var Q32;
            Q32=makeQuery(id+"F21.opExtrude","CAP_EDGE",EDGE,{"disambiguationData":[OSD([sQuery(id+"F20.wireOp",EDGE,"E66")])],"isStart":true});
            var Q33;
            Q33=makeQuery(id+"F21.opExtrude","CAP_EDGE",EDGE,{"disambiguationData":[OSD([sQuery(id+"F20.wireOp",EDGE,"E59")])],"isStart":true});
            var Q34;
            Q34=makeQuery(id+"F23.opPattern","COPY",EDGE,{"derivedFrom":makeQuery(id+"F18.opExtrude","CAP_EDGE",EDGE,{"disambiguationData":[OSD([sQuery(id+"F13.wireOp",EDGE,"E42")])],"isStart":true}),"instanceName":"1"});
            var Q35;
            Q35=makeQuery(id+"F23.opPattern","COPY",EDGE,{"derivedFrom":makeQuery(id+"F18.opExtrude","CAP_EDGE",EDGE,{"disambiguationData":[OSD([sQuery(id+"F13.wireOp",EDGE,"E31.0")])],"isStart":true}),"instanceName":"1"});
            var Q36;
            Q36=makeQuery(id+"F23.opPattern","COPY",EDGE,{"derivedFrom":makeQuery(id+"F18.opExtrude","CAP_EDGE",EDGE,{"disambiguationData":[OSD([sQuery(id+"F13.wireOp",EDGE,"E34")])],"isStart":true}),"instanceName":"1"});
            var Q37;
            Q37=makeQuery(id+"F23.opPattern","COPY",EDGE,{"derivedFrom":makeQuery(id+"F18.opExtrude","CAP_EDGE",EDGE,{"disambiguationData":[OSD([sQuery(id+"F13.wireOp",EDGE,"E30.0")])],"isStart":true}),"instanceName":"1"});
            var Q38;
            Q38=makeQuery(id+"F23.opPattern","COPY",EDGE,{"derivedFrom":makeQuery(id+"F18.opExtrude","CAP_EDGE",EDGE,{"disambiguationData":[OSD([sQuery(id+"F13.wireOp",EDGE,"E32.bottom")])],"isStart":true}),"instanceName":"1"});
            var Q39;
            Q39=makeQuery(id+"F23.opPattern","COPY",EDGE,{"derivedFrom":makeQuery(id+"F18.opExtrude","CAP_EDGE",EDGE,{"disambiguationData":[OSD([sQuery(id+"F13.wireOp",EDGE,"E48")])],"isStart":true}),"instanceName":"1"});
            var Q40;
            Q40=makeQuery(id+"F23.opPattern","COPY",EDGE,{"derivedFrom":makeQuery(id+"F18.opExtrude","CAP_EDGE",EDGE,{"disambiguationData":[OSD([sQuery(id+"F13.wireOp",EDGE,"E46")])],"isStart":true}),"instanceName":"1"});
            var Q41;
            Q41=makeQuery(id+"F23.opPattern","COPY",EDGE,{"derivedFrom":makeQuery(id+"F18.opExtrude","CAP_EDGE",EDGE,{"disambiguationData":[OSD([sQuery(id+"F13.wireOp",EDGE,"E49")])],"isStart":true}),"instanceName":"1"});
            var Q42;
            Q42=makeQuery(id+"F23.opPattern","COPY",EDGE,{"derivedFrom":makeQuery(id+"F18.opExtrude","CAP_EDGE",EDGE,{"disambiguationData":[OSD([sQuery(id+"F13.wireOp",EDGE,"E32.bottom"),sQuery(id+"F13.wireOp",EDGE,"E41")])],"isStart":true}),"instanceName":"1"});
            var Q43;
            Q43=makeQuery(id+"F23.opPattern","COPY",EDGE,{"derivedFrom":makeQuery(id+"F18.opExtrude","CAP_EDGE",EDGE,{"disambiguationData":[OSD([sQuery(id+"F13.wireOp",EDGE,"E33")])],"isStart":true}),"instanceName":"1"});
            var Q44;
            Q44=makeQuery(id+"F30.opExtrude","CAP_EDGE",EDGE,{"disambiguationData":[OSD([sQuery(id+"F29.wireOp",EDGE,"on8Fqwfm-eHCa-UyCz-5yqo-W9CwT8bCkcOa")])],"isStart":true});
            var Q45;
            Q45=makeQuery(id+"F30.opExtrude","CAP_EDGE",EDGE,{"disambiguationData":[OSD([sQuery(id+"F29.wireOp",EDGE,"E90")])],"isStart":true});
            var Q46;
            Q46=makeQuery(id+"F30.opExtrude","CAP_EDGE",EDGE,{"disambiguationData":[OSD([sQuery(id+"F29.wireOp",EDGE,"E77.0")])],"isStart":true});
            chamfer(context, id + "F39", {"entities" : qUnion([Q0, Q1, Q2, Q3, Q4, Q5, Q6, Q7, Q8, Q9, Q10, Q11, Q12, Q13, Q14, Q15, Q16, Q17, Q18, Q19, Q20, Q21, Q22, Q23, Q24, Q25, Q26, Q27, Q28, Q29, Q30, Q31, Q32, Q33, Q34, Q35, Q36, Q37, Q38, Q39, Q40, Q41, Q42, Q43, Q44, Q45, Q46]), "chamferType" : ChamferType.TWO_OFFSETS, "width1" : .35 * mm, "oppositeDirection" : true, "width2" : 1.5 * mm, "tangentPropagation" : true});
        }
    });
